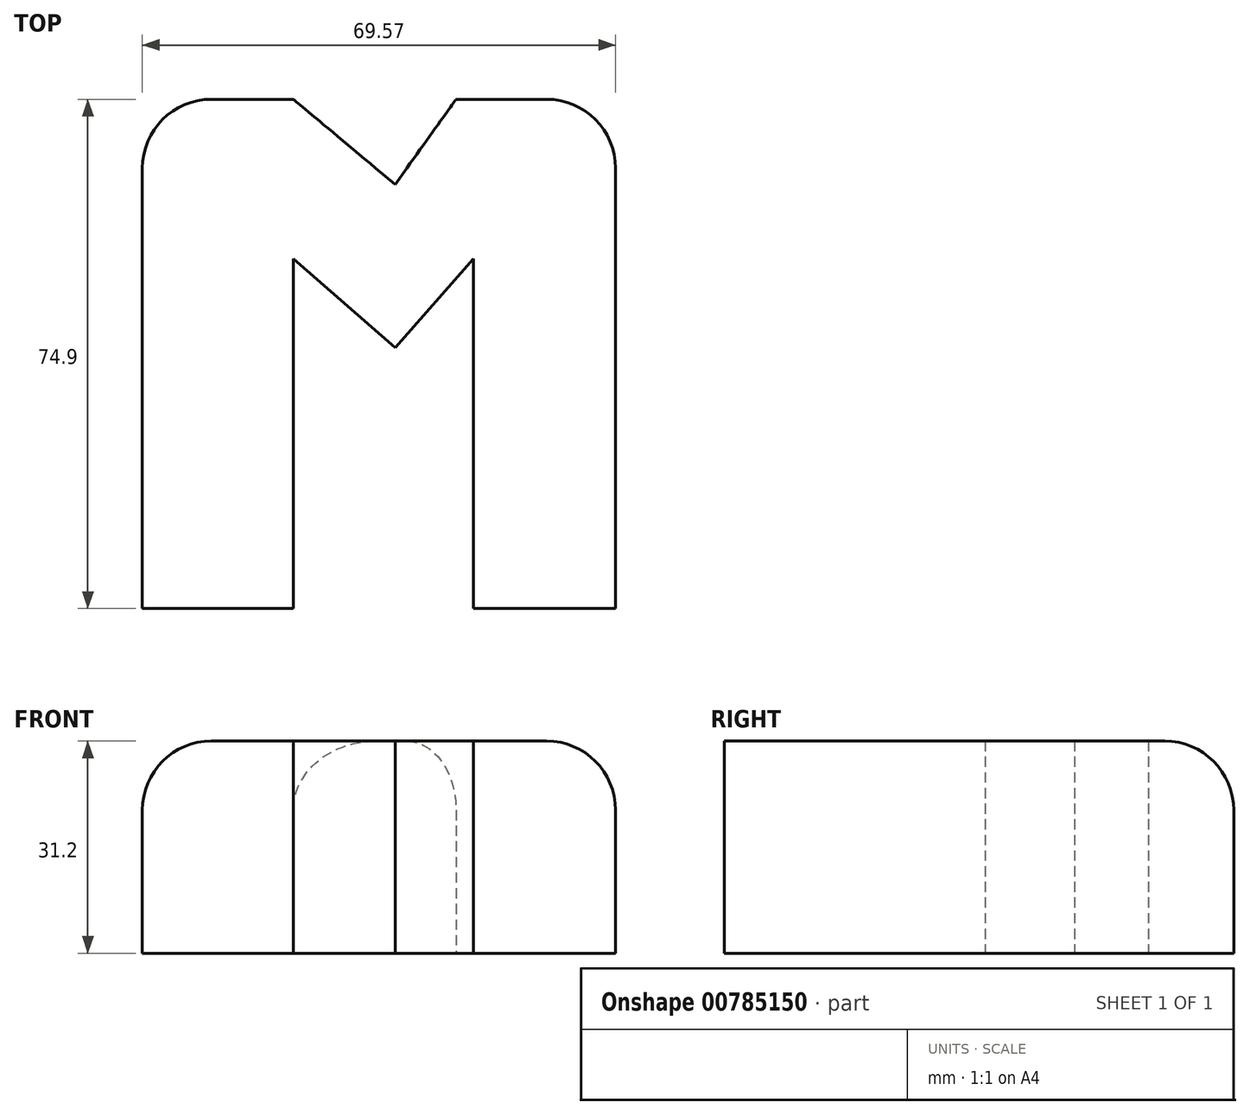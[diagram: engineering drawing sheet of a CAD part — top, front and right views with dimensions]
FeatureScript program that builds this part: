
annotation { "Feature Type Name" : "Feature", "Feature Type Description" : "" }
export const myFeature = defineFeature(function(context is Context, id is Id, definition is map)
    precondition{}
    {
        {
            var Q0;
            Q0=qCreatedBy(makeId("Top.planeOp"),FACE);
            var sketch = newSketch(context, id + "F0", { "sketchPlane" : qUnion([Q0])});
            skLineSegment(sketch, "E0.bottom", {"start": v(-74.75, 74.46) * mm, "end": v(74.75, 74.46) * mm});
            skLineSegment(sketch, "E0.top", {"start": v(-74.75, -75.05) * mm, "end": v(74.75, -75.05) * mm});
            skLineSegment(sketch, "E0.left", {"start": v(-74.75, 74.46) * mm, "end": v(-74.75, -75.05) * mm});
            skLineSegment(sketch, "E0.right", {"start": v(74.75, 74.46) * mm, "end": v(74.75, -75.05) * mm});
            skLineSegment(sketch, "E1", {"start": v(-37.15, 36.56) * mm, "end": v(-37.15, -38.34) * mm});
            skLineSegment(sketch, "E2", {"start": v(-37.15, -38.34) * mm, "end": v(-14.95, -38.34) * mm});
            skLineSegment(sketch, "E3", {"start": v(-14.95, -38.34) * mm, "end": v(-14.95, 13.13) * mm});
            skLineSegment(sketch, "E4", {"start": v(-14.95, 13.13) * mm, "end": v(0, 0) * mm});
            skLineSegment(sketch, "E5", {"start": v(-37.15, 36.56) * mm, "end": v(-14.95, 36.56) * mm});
            skLineSegment(sketch, "E6", {"start": v(-14.95, 36.56) * mm, "end": v(0, 24.03) * mm});
            skLineSegment(sketch, "E7", {"start": v(0, 24.03) * mm, "end": v(8.97, 36.56) * mm});
            skLineSegment(sketch, "E8", {"start": v(0, 0) * mm, "end": v(11.53, 13.13) * mm});
            skLineSegment(sketch, "E9", {"start": v(11.53, 13.13) * mm, "end": v(11.53, -38.34) * mm});
            skLineSegment(sketch, "E10", {"start": v(11.53, -38.34) * mm, "end": v(32.42, -38.34) * mm});
            skLineSegment(sketch, "E11", {"start": v(32.42, -38.34) * mm, "end": v(32.42, 36.56) * mm});
            skLineSegment(sketch, "E12", {"start": v(32.42, 36.56) * mm, "end": v(8.97, 36.56) * mm});
            skSolve(sketch);
        }
        {
            var Q0;
            Q0=makeQuery(id+"F0.imprint","IMPRINT",FACE,{"disambiguationData":[TD([[makeQuery(id+"F0.imprint","IMPRINT",EDGE,{"derivedFrom":sQuery(id+"F0.wireOp",EDGE,"E1")}),1.0]])]});
            extrude(context, id + "F1", {"entities" : qUnion([Q0]), "depth" : 15.9 * mm, "offsetDistance" : 25 * mm});
        }
        {
            var Q0;
            Q0=makeQuery(id+"F1.opExtrude","CAP_FACE",FACE,{"disambiguationData":[OSD([sQuery(id+"F0.wireOp",EDGE,"E1"),sQuery(id+"F0.wireOp",EDGE,"E2"),sQuery(id+"F0.wireOp",EDGE,"E3"),sQuery(id+"F0.wireOp",EDGE,"E4"),sQuery(id+"F0.wireOp",EDGE,"E5"),sQuery(id+"F0.wireOp",EDGE,"E6"),sQuery(id+"F0.wireOp",EDGE,"E7"),sQuery(id+"F0.wireOp",EDGE,"E8"),sQuery(id+"F0.wireOp",EDGE,"E9"),sQuery(id+"F0.wireOp",EDGE,"E10"),sQuery(id+"F0.wireOp",EDGE,"E11"),sQuery(id+"F0.wireOp",EDGE,"E12")])],"isStart":false});
            extrude(context, id + "F2", {"entities" : qUnion([Q0]), "operationType" : NewBodyOperationType.ADD, "oppositeDirection" : true, "depth" : 31.2 * mm, "offsetDistance" : 25 * mm});
        }
        {
            var Q0;
            Q0=makeQuery(id+"F1.opExtrude","CAP_EDGE",EDGE,{"disambiguationData":[OSD([sQuery(id+"F0.wireOp",EDGE,"E5")])],"isStart":false});
            var Q1;
            Q1=makeQuery(id+"F1.opExtrude","CAP_EDGE",EDGE,{"disambiguationData":[OSD([sQuery(id+"F0.wireOp",EDGE,"E12")])],"isStart":false});
            var Q2;
            Q2=makeQuery(id+"F1.opExtrude","CAP_EDGE",EDGE,{"disambiguationData":[OSD([sQuery(id+"F0.wireOp",EDGE,"E11")])],"isStart":false});
            var Q3;
            Q3=makeQuery(id+"F1.opExtrude","CAP_EDGE",EDGE,{"disambiguationData":[OSD([sQuery(id+"F0.wireOp",EDGE,"E1")])],"isStart":false});
            var Q4;
            {var subQ0=sQuery(id+"F0.wireOp",EDGE,"E5");var subQ1=sQuery(id+"F0.wireOp",EDGE,"E1");Q4=makeQuery(id+"F2.boolean.opBoolean","MERGE",EDGE,{"derivedFrom":[makeQuery(id+"F1.opExtrude","SWEPT_EDGE",EDGE,{"disambiguationData":[OSD([subQ1,subQ0])]}),makeQuery(id+"F2.opExtrude","SWEPT_EDGE",EDGE,{"disambiguationData":[OSD([subQ1,subQ0])]})]});}
            var Q5;
            {var subQ0=sQuery(id+"F0.wireOp",EDGE,"E12");var subQ1=sQuery(id+"F0.wireOp",EDGE,"E11");Q5=makeQuery(id+"F2.boolean.opBoolean","MERGE",EDGE,{"derivedFrom":[makeQuery(id+"F1.opExtrude","SWEPT_EDGE",EDGE,{"disambiguationData":[OSD([subQ1,subQ0])]}),makeQuery(id+"F2.opExtrude","SWEPT_EDGE",EDGE,{"disambiguationData":[OSD([subQ1,subQ0])]})]});}
            fillet(context, id + "F3", {"entities" : qUnion([Q0, Q1, Q2, Q3, Q4, Q5]), "radius" : 10.14 * mm, "tangentPropagation" : true, "allowEdgeOverflow" : false});
        }
    });
